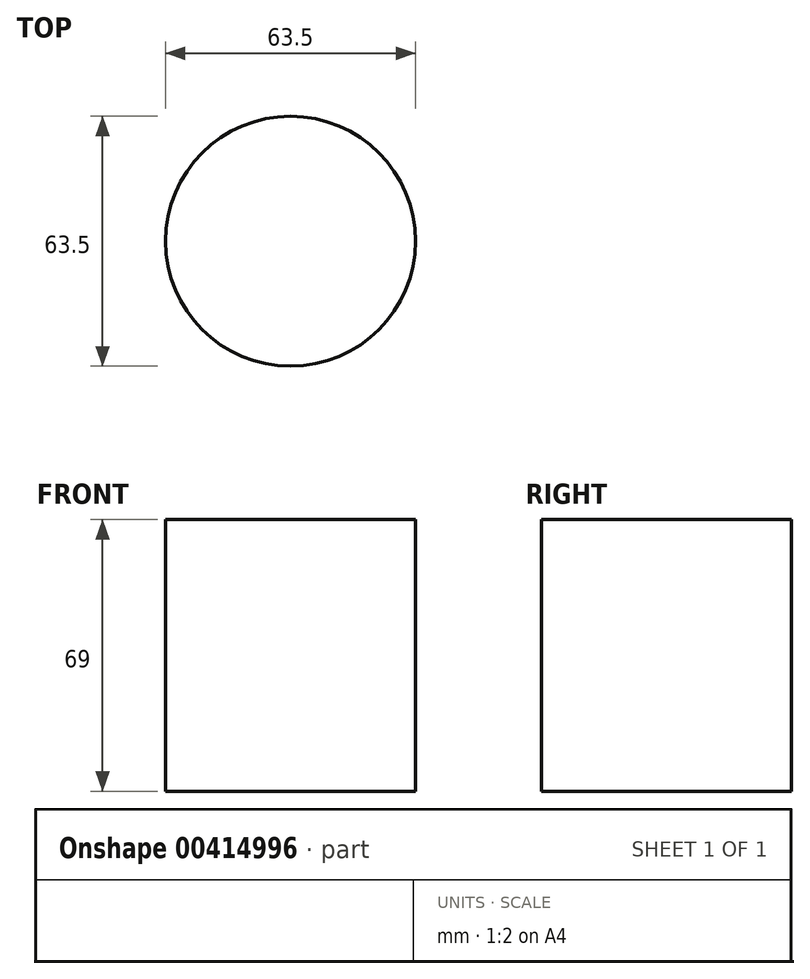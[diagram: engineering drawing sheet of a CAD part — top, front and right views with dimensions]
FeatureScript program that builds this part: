
annotation { "Feature Type Name" : "Feature", "Feature Type Description" : "" }
export const myFeature = defineFeature(function(context is Context, id is Id, definition is map)
    precondition{}
    {
        {
            var Q0;
            Q0=qCreatedBy(makeId("Top.planeOp"),FACE);
            var sketch = newSketch(context, id + "F0", { "sketchPlane" : qUnion([Q0])});
            skCircle(sketch, "E0", {"center": v(0, 0) * mm, "radius": 31.75 * mm});
            skSolve(sketch);
        }
        {
            var Q0;
            Q0=makeQuery(id+"F0.imprint","IMPRINT",FACE,{"disambiguationData":[TD([[makeQuery(id+"F0.imprint","IMPRINT",EDGE,{"derivedFrom":sQuery(id+"F0.wireOp",EDGE,"E0")}),1.0]])]});
            extrude(context, id + "F1", {"entities" : qUnion([Q0]), "depth" : 69 * mm});
        }
    });
